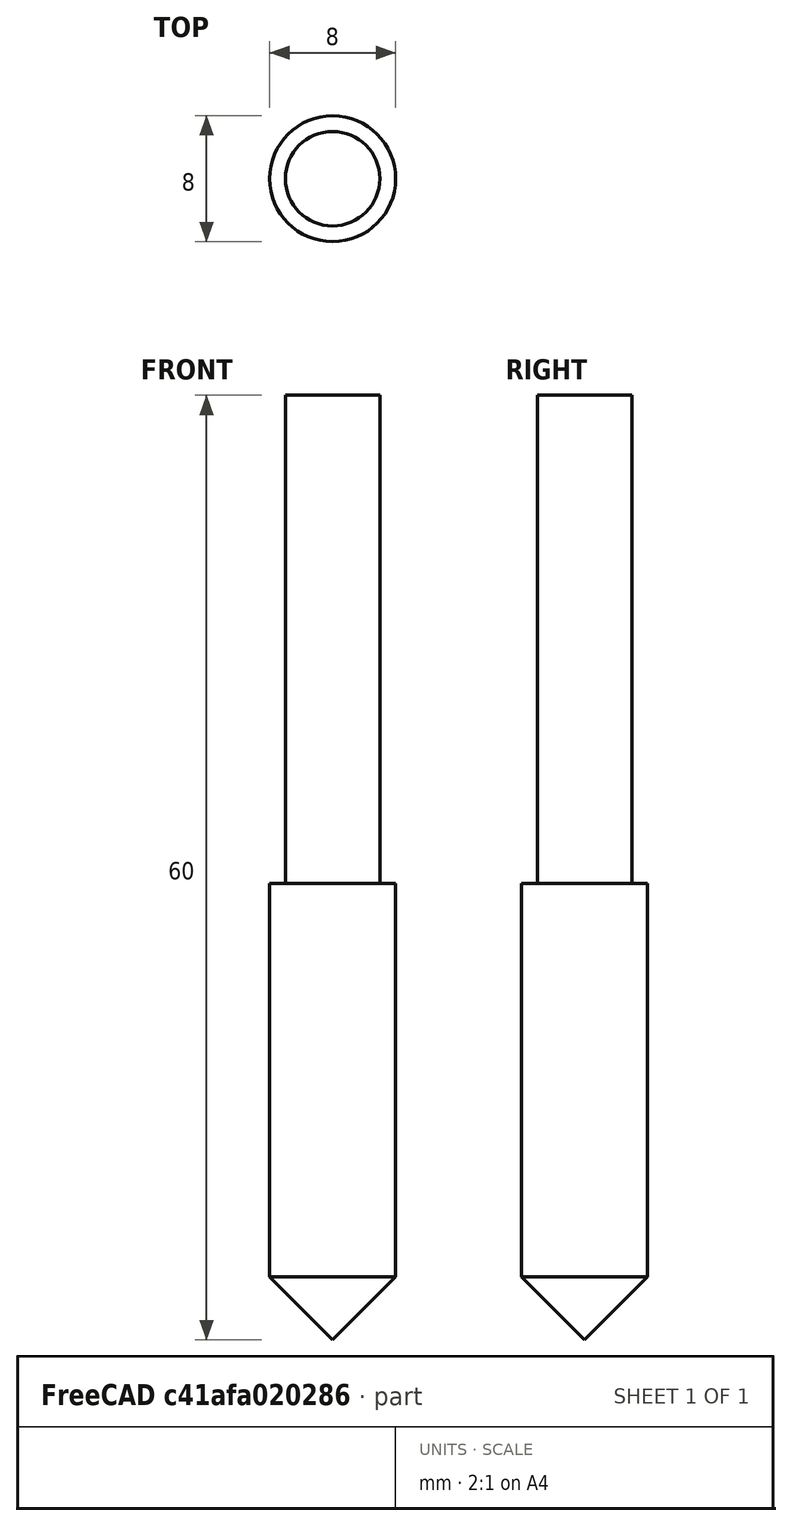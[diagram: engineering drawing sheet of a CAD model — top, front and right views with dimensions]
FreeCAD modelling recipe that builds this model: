
FCSTD DOCUMENT  (FreeCAD 1.1R43556 +51 (Git))
Label: tap
License: All rights reserved
LicenseURL: http://en.wikipedia.org/wiki/All_rights_reserved
objects: Sketcher::SketchObject×1, PartDesign::Revolution×1, App::FeaturePython×1, PartDesign::Body×1, App::Point×1
note: 6 computed .brp shape members not serialized (recipe doc carries the construction recipe); baked Part::Feature solids carry a one-line shape summary decoded from their .brp

FEATURE [Sketcher::SketchObject] Sketch
  ArcFitTolerance = 0
  AttachmentSupport = -> [XZ_Plane]
  ExternalTypes = [0]
  FullyConstrained = true
  MakeInternals = false
  MapMode = 5
  Placement = pos=(0,0,0) rot=(1,0,0;1.5708rad)
  expr: Constraints[14] = <<Attributes>>.CuttingEdgeLength
  expr: Constraints[17] = <<Attributes>>.Diameter
  expr: Constraints[18] = <<Attributes>>.ShankDiameter
  expr: Constraints[19] = <<Attributes>>.Length
  expr: Constraints[21] = <<Attributes>>.TipAngle
  sketch-geometry (9):
    g0: LineSegment StartX=0 StartY=0 StartZ=0 EndX=4 EndY=4 EndZ=0
    g1: LineSegment StartX=4 StartY=4 StartZ=0 EndX=4 EndY=29 EndZ=0
    g2: LineSegment StartX=4 StartY=29 StartZ=0 EndX=3 EndY=29 EndZ=0
    g3: LineSegment StartX=3 StartY=29 StartZ=0 EndX=3 EndY=60 EndZ=0
    g4: LineSegment StartX=3 StartY=60 StartZ=0 EndX=0 EndY=60 EndZ=0
    g5: LineSegment StartX=0 StartY=60 StartZ=0 EndX=0 EndY=0 EndZ=0
    g6: LineSegment [constr] StartX=-3 StartY=60 StartZ=0 EndX=3 EndY=60 EndZ=0
    g7: LineSegment [constr] StartX=4 StartY=29 StartZ=0 EndX=-4 EndY=29 EndZ=0
    g8: LineSegment [constr] StartX=0 StartY=0 StartZ=0 EndX=-4 EndY=4 EndZ=0
  constraints (23):
    c: Coincident(g-1,g0)
    c: Coincident(g0,g1)
    c: Vertical(g1)
    c: Coincident(g1,g2)
    c: Horizontal(g2)
    c: Coincident(g2,g3)
    c: Vertical(g3)
    c: Coincident(g3,g4)
    c: Horizontal(g4)
    c: Coincident(g4,g5)
    c: Coincident(g5,g0)
    c: Vertical(g5)
    c: Symmetric(g6,g6,g-2)
    c: Coincident(g6,g3)
    c: DistanceY(g1,g1) = 25
    c: Symmetric(g7,g7,g-2)
    c: Coincident(g7,g1)
    c: DistanceX(g7,g7) = 8
    c: DistanceX(g6,g3) = 6
    c: DistanceY(g5,g5) = 60
    c: Coincident(g8,g0)
    c: Angle(g0,g8) = 1.5708
    c: Symmetric(g0,g8,g5)
FEATURE [PartDesign::Revolution] Revolution
  Angle = 360
  Angle2 = 60
  Axis = (0,2e-16,1)
  Base = (0,0,0)
  Placement = pos=(0,0,0) rot=(1,0,0;1.5708rad)
  Profile = -> Sketch
  ReferenceAxis = -> Sketch [V_Axis]
  Reversed = true
  Suppressed = false
  Type = 0
FEATURE [App::FeaturePython] PropertyBag  label="Attributes"  # WARN: FeaturePython — macro-defined, semantics opaque (R4)
  CustomPropertyGroups = 0
  CuttingEdgeLength = 25
  Diameter = 8
  Flutes = 4
  Length = 60
  Pitch = 0
  ShankDiameter = 6
  TipAngle = 90
FEATURE [PartDesign::Body] Body  label="Tap"
  AllowCompound = false
  Group = -> [Sketch,Revolution,PropertyBag]
  Origin = -> Origin
  Tip = -> Revolution
FEATURE [App::Point] Origin001  label="Origin"
  Role = Origin
